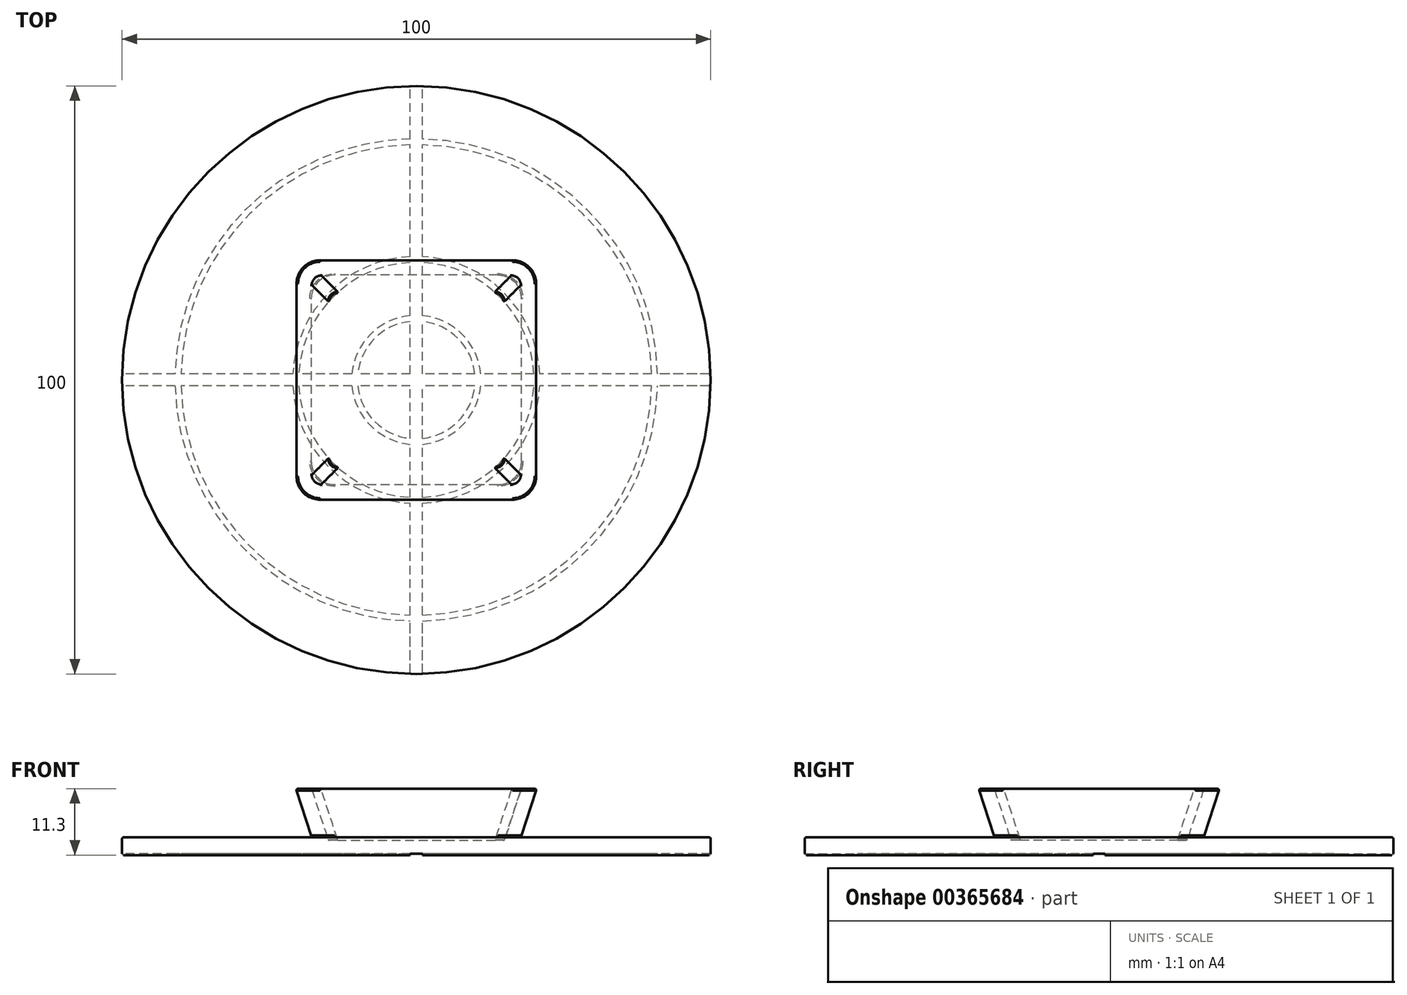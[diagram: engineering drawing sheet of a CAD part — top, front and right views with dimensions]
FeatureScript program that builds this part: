
annotation { "Feature Type Name" : "Feature", "Feature Type Description" : "" }
export const myFeature = defineFeature(function(context is Context, id is Id, definition is map)
    precondition{}
    {
        {
            var Q0;
            Q0=qCreatedBy(makeId("Top.planeOp"),FACE);
            cPlane(context, id + "F0", {"entities" : qUnion([Q0]), "cplaneType" : CPlaneType.OFFSET, "offset" : 8.3 * mm, "width" : 150 * mm, "height" : 150 * mm});
        }
        {
            var Q0;
            Q0=qCreatedBy(makeId("Top.planeOp"),FACE);
            var sketch = newSketch(context, id + "F1", { "sketchPlane" : qUnion([Q0])});
            skLineSegment(sketch, "E0.bottom", {"start": v(-13.75, 17.75) * mm, "end": v(13.75, 17.75) * mm});
            skLineSegment(sketch, "E0.top", {"start": v(-13.75, -17.75) * mm, "end": v(13.75, -17.75) * mm});
            skLineSegment(sketch, "E0.left", {"start": v(-17.75, 13.75) * mm, "end": v(-17.75, -13.75) * mm});
            skLineSegment(sketch, "E0.right", {"start": v(17.75, 13.75) * mm, "end": v(17.75, -13.75) * mm});
            skPoint(sketch, "E0.middle", {"position": v(0, 0) * mm});
            skPoint(sketch, "E1.visualSharp", {"position": v(-17.75, 17.75) * mm});
            skArc(sketch, "E1.filletArc", {"start": v(-13.75, 17.75) * mm, "mid": v(-16.58, 16.58) * mm, "end": v(-17.75, 13.75) * mm});
            skPoint(sketch, "E2.visualSharp", {"position": v(17.75, 17.75) * mm});
            skArc(sketch, "E2.filletArc", {"start": v(17.75, 13.75) * mm, "mid": v(16.58, 16.58) * mm, "end": v(13.75, 17.75) * mm});
            skPoint(sketch, "E3.visualSharp", {"position": v(17.75, -17.75) * mm});
            skArc(sketch, "E3.filletArc", {"start": v(13.75, -17.75) * mm, "mid": v(16.58, -16.58) * mm, "end": v(17.75, -13.75) * mm});
            skPoint(sketch, "E4.visualSharp", {"position": v(-17.75, -17.75) * mm});
            skArc(sketch, "E4.filletArc", {"start": v(-17.75, -13.75) * mm, "mid": v(-16.58, -16.58) * mm, "end": v(-13.75, -17.75) * mm});
            skSolve(sketch);
        }
        {
            var Q0;
            Q0=qCreatedBy(id+"F0.planeOp",FACE);
            var sketch = newSketch(context, id + "F2", { "sketchPlane" : qUnion([Q0])});
            skLineSegment(sketch, "E5.bottom", {"start": v(-16.45, 20.45) * mm, "end": v(16.45, 20.45) * mm});
            skLineSegment(sketch, "E5.top", {"start": v(-16.45, -20.45) * mm, "end": v(16.45, -20.45) * mm});
            skLineSegment(sketch, "E5.left", {"start": v(-20.45, 16.45) * mm, "end": v(-20.45, -16.45) * mm});
            skLineSegment(sketch, "E5.right", {"start": v(20.45, 16.45) * mm, "end": v(20.45, -16.45) * mm});
            skPoint(sketch, "E5.middle", {"position": v(0, 0) * mm});
            skPoint(sketch, "E6.visualSharp", {"position": v(-20.45, 20.45) * mm});
            skArc(sketch, "E6.filletArc", {"start": v(-16.45, 20.45) * mm, "mid": v(-19.28, 19.28) * mm, "end": v(-20.45, 16.45) * mm});
            skPoint(sketch, "E7.visualSharp", {"position": v(20.45, 20.45) * mm});
            skArc(sketch, "E7.filletArc", {"start": v(20.45, 16.45) * mm, "mid": v(19.28, 19.28) * mm, "end": v(16.45, 20.45) * mm});
            skPoint(sketch, "E8.visualSharp", {"position": v(20.45, -20.45) * mm});
            skArc(sketch, "E8.filletArc", {"start": v(16.45, -20.45) * mm, "mid": v(19.28, -19.28) * mm, "end": v(20.45, -16.45) * mm});
            skPoint(sketch, "E9.visualSharp", {"position": v(-20.45, -20.45) * mm});
            skArc(sketch, "E9.filletArc", {"start": v(-20.45, -16.45) * mm, "mid": v(-19.28, -19.28) * mm, "end": v(-16.45, -20.45) * mm});
            skSolve(sketch);
        }
        {
            var Q0;
            Q0 = qSketchRegion(id + "F1", true);
            var Q1;
            Q1 = qSketchRegion(id + "F2", true);
            loft(context, id + "F3", {"sheetProfilesArray" : [{ "sheetProfileEntities" : qUnion([Q0]) }, { "sheetProfileEntities" : qUnion([Q1]) }]});
        }
        {
            var Q0;
            Q0=qCreatedBy(makeId("Top.planeOp"),FACE);
            var sketch = newSketch(context, id + "F4", { "sketchPlane" : qUnion([Q0])});
            skCircle(sketch, "E10", {"center": v(0, 0) * mm, "radius": 50 * mm});
            skSolve(sketch);
        }
        {
            var Q0;
            Q0 = qSketchRegion(id + "F4", true);
            extrude(context, id + "F5", {"entities" : qUnion([Q0]), "operationType" : NewBodyOperationType.ADD, "oppositeDirection" : true, "depth" : 3 * mm});
        }
        {
            var Q0;
            Q0=makeQuery(id+"F3.opLoft","CAP_FACE",FACE,{"disambiguationData":[OSD([makeQuery(id+"F2.imprint","IMPRINT",FACE,{"disambiguationData":[TD([[makeQuery(id+"F2.imprint","IMPRINT",EDGE,{"derivedFrom":sQuery(id+"F2.wireOp",EDGE,"E5.bottom")}),-1.0]])]})])],"isStart":true});
            shell(context, id + "F6", {"entities" : qUnion([Q0]), "thickness" : 2.5 * mm});
        }
        {
            var Q0;
            Q0=makeQuery(id+"F3.opLoft","CAP_FACE",FACE,{"disambiguationData":[OSD([makeQuery(id+"F2.imprint","IMPRINT",FACE,{"disambiguationData":[TD([[makeQuery(id+"F2.imprint","IMPRINT",EDGE,{"derivedFrom":sQuery(id+"F2.wireOp",EDGE,"E5.bottom")}),-1.0]])]})])],"isStart":true});
            var Q1;
            Q1=makeQuery(id+"F5.opExtrude","CAP_FACE",FACE,{"disambiguationData":[OSD([sQuery(id+"F4.wireOp",EDGE,"E10")])],"isStart":true});
            var Q2;
            Q2=makeQuery(id+"F5.opExtrude","CAP_FACE",FACE,{"disambiguationData":[OSD([sQuery(id+"F4.wireOp",EDGE,"E10")])],"isStart":false});
            var Q3;
            Q3=makeQuery(id+"F6.opShell","OFFSET_FACE",FACE,{"disambiguationData":[OSD([sQuery(id+"F4.wireOp",EDGE,"E10")])]});
            fillet(context, id + "F7", {"entities" : qUnion([Q0, Q1, Q2, Q3]), "radius" : .25 * mm, "tangentPropagation" : true, "allowEdgeOverflow" : false});
        }
        {
            var Q0;
            Q0=makeQuery(id+"F5.opExtrude","CAP_FACE",FACE,{"disambiguationData":[OSD([sQuery(id+"F4.wireOp",EDGE,"E10")])],"isStart":false});
            cPlane(context, id + "F8", {"entities" : qUnion([Q0]), "cplaneType" : CPlaneType.OFFSET, "offset" : .25 * mm, "oppositeDirection" : true, "width" : 150 * mm, "height" : 150 * mm});
        }
        {
            var Q0;
            Q0=qCreatedBy(id+"F8.planeOp",FACE);
            var sketch = newSketch(context, id + "F9", { "sketchPlane" : qUnion([Q0])});
            skArc(sketch, "E11", {"start": v(-9.95, -1) * mm, "mid": v(-7.09, -7.06) * mm, "end": v(-1.04, -9.95) * mm});
            skArc(sketch, "E12", {"start": v(-10.95, -1) * mm, "mid": v(-7.8, -7.76) * mm, "end": v(-1.04, -10.95) * mm});
            skLineSegment(sketch, "E13.bottom", {"start": v(-1.04, 55) * mm, "end": v(1.04, 55) * mm});
            skLineSegment(sketch, "E13.top", {"start": v(-1.04, -55) * mm, "end": v(1.04, -55) * mm});
            skLineSegment(sketch, "E13.left", {"start": v(-1.04, 55) * mm, "end": v(-1.04, 40.99) * mm});
            skLineSegment(sketch, "E13.right", {"start": v(1.04, 55) * mm, "end": v(1.04, 40.99) * mm});
            skLineSegment(sketch, "E14.bottom", {"start": v(55, -1) * mm, "end": v(40.99, -1) * mm});
            skLineSegment(sketch, "E14.top", {"start": v(55, 1) * mm, "end": v(40.99, 1) * mm});
            skLineSegment(sketch, "E14.left", {"start": v(55, -1) * mm, "end": v(55, 1) * mm});
            skLineSegment(sketch, "E14.right", {"start": v(-55, -1) * mm, "end": v(-55, 1) * mm});
            skArc(sketch, "E15", {"start": v(-19.97, -1) * mm, "mid": v(-14.16, -14.13) * mm, "end": v(-1.04, -19.97) * mm});
            skArc(sketch, "E16", {"start": v(-20.98, -1) * mm, "mid": v(-14.86, -14.84) * mm, "end": v(-1.04, -20.97) * mm});
            skArc(sketch, "E17", {"start": v(-39.99, -1) * mm, "mid": v(-28.3, -28.27) * mm, "end": v(-1.04, -39.99) * mm});
            skArc(sketch, "E18", {"start": v(-40.99, -1) * mm, "mid": v(-29, -28.98) * mm, "end": v(-1.04, -40.99) * mm});
            skLineSegment(sketch, "E19.trimOffspring", {"start": v(-40.99, 1) * mm, "end": v(-55, 1) * mm});
            skLineSegment(sketch, "E20.trimOffspring", {"start": v(-40.99, -1) * mm, "end": v(-55, -1) * mm});
            skLineSegment(sketch, "E21.trimOffspring", {"start": v(-20.98, -1) * mm, "end": v(-39.99, -1) * mm});
            skLineSegment(sketch, "E22.trimOffspring", {"start": v(-20.98, 1) * mm, "end": v(-39.99, 1) * mm});
            skLineSegment(sketch, "E23.trimOffspring", {"start": v(-10.95, 1) * mm, "end": v(-19.97, 1) * mm});
            skLineSegment(sketch, "E24.trimOffspring", {"start": v(-10.95, -1) * mm, "end": v(-19.97, -1) * mm});
            skArc(sketch, "E25.trimOffspring", {"start": v(1.04, -40.99) * mm, "mid": v(29, -28.98) * mm, "end": v(40.99, -1) * mm});
            skLineSegment(sketch, "E26.trimOffspring", {"start": v(-1.04, -40.99) * mm, "end": v(-1.04, -55) * mm});
            skArc(sketch, "E27.trimOffspring", {"start": v(1.04, -39.99) * mm, "mid": v(28.3, -28.27) * mm, "end": v(39.99, -1) * mm});
            skLineSegment(sketch, "E28.trimOffspring", {"start": v(1.04, -40.99) * mm, "end": v(1.04, -55) * mm});
            skLineSegment(sketch, "E29.trimOffspring", {"start": v(1.04, -20.97) * mm, "end": v(1.04, -39.99) * mm});
            skLineSegment(sketch, "E30.trimOffspring", {"start": v(-1.04, -20.97) * mm, "end": v(-1.04, -39.99) * mm});
            skArc(sketch, "E31.trimOffspring", {"start": v(1.04, -19.97) * mm, "mid": v(14.16, -14.13) * mm, "end": v(19.97, -1) * mm});
            skArc(sketch, "E32.trimOffspring", {"start": v(1.04, -20.97) * mm, "mid": v(14.86, -14.84) * mm, "end": v(20.98, -1) * mm});
            skLineSegment(sketch, "E33.trimOffspring", {"start": v(-1.04, -1) * mm, "end": v(-9.95, -1) * mm});
            skLineSegment(sketch, "E34.trimOffspring", {"start": v(-1.04, 1) * mm, "end": v(-9.95, 1) * mm});
            skLineSegment(sketch, "E35.trimOffspring", {"start": v(-1.04, -1) * mm, "end": v(-1.04, -9.95) * mm});
            skLineSegment(sketch, "E36.trimOffspring", {"start": v(1.04, -1) * mm, "end": v(1.04, -9.95) * mm});
            skArc(sketch, "E37.trimOffspring", {"start": v(1.04, -9.95) * mm, "mid": v(7.09, -7.06) * mm, "end": v(9.95, -1) * mm});
            skArc(sketch, "E38.trimOffspring", {"start": v(1.04, -10.95) * mm, "mid": v(7.8, -7.76) * mm, "end": v(10.95, -1) * mm});
            skLineSegment(sketch, "E39.trimOffspring", {"start": v(-1.04, -10.95) * mm, "end": v(-1.04, -19.97) * mm});
            skLineSegment(sketch, "E40.trimOffspring", {"start": v(1.04, -10.95) * mm, "end": v(1.04, -19.97) * mm});
            skLineSegment(sketch, "E41.trimOffspring", {"start": v(9.95, -1) * mm, "end": v(1.04, -1) * mm});
            skLineSegment(sketch, "E42.trimOffspring", {"start": v(9.95, 1) * mm, "end": v(1.04, 1) * mm});
            skArc(sketch, "E43.trimOffspring", {"start": v(9.95, 1) * mm, "mid": v(7.09, 7.06) * mm, "end": v(1.04, 9.95) * mm});
            skArc(sketch, "E44.trimOffspring", {"start": v(10.95, 1) * mm, "mid": v(7.8, 7.76) * mm, "end": v(1.04, 10.95) * mm});
            skArc(sketch, "E45.trimOffspring", {"start": v(20.98, 1) * mm, "mid": v(14.86, 14.84) * mm, "end": v(1.04, 20.97) * mm});
            skArc(sketch, "E46.trimOffspring", {"start": v(19.97, 1) * mm, "mid": v(14.16, 14.13) * mm, "end": v(1.04, 19.97) * mm});
            skLineSegment(sketch, "E47.trimOffspring", {"start": v(19.97, -1) * mm, "end": v(10.95, -1) * mm});
            skLineSegment(sketch, "E48.trimOffspring", {"start": v(19.97, 1) * mm, "end": v(10.95, 1) * mm});
            skLineSegment(sketch, "E49.trimOffspring", {"start": v(39.99, -1) * mm, "end": v(20.98, -1) * mm});
            skArc(sketch, "E50.trimOffspring", {"start": v(40.99, 1) * mm, "mid": v(29, 28.98) * mm, "end": v(1.04, 40.99) * mm});
            skArc(sketch, "E51.trimOffspring", {"start": v(39.99, 1) * mm, "mid": v(28.3, 28.27) * mm, "end": v(1.04, 39.99) * mm});
            skLineSegment(sketch, "E52.trimOffspring", {"start": v(39.99, 1) * mm, "end": v(20.98, 1) * mm});
            skArc(sketch, "E53.trimOffspring", {"start": v(-1.04, 40.99) * mm, "mid": v(-29, 28.98) * mm, "end": v(-40.99, 1) * mm});
            skArc(sketch, "E54.trimOffspring", {"start": v(-1.04, 39.99) * mm, "mid": v(-28.3, 28.27) * mm, "end": v(-39.99, 1) * mm});
            skLineSegment(sketch, "E55.trimOffspring", {"start": v(-1.04, 39.99) * mm, "end": v(-1.04, 20.97) * mm});
            skLineSegment(sketch, "E56.trimOffspring", {"start": v(1.04, 39.99) * mm, "end": v(1.04, 20.97) * mm});
            skArc(sketch, "E57.trimOffspring", {"start": v(-1.04, 19.97) * mm, "mid": v(-14.16, 14.13) * mm, "end": v(-19.97, 1) * mm});
            skArc(sketch, "E58.trimOffspring", {"start": v(-1.04, 20.97) * mm, "mid": v(-14.86, 14.84) * mm, "end": v(-20.98, 1) * mm});
            skLineSegment(sketch, "E59.trimOffspring", {"start": v(1.04, 19.97) * mm, "end": v(1.04, 10.95) * mm});
            skLineSegment(sketch, "E60.trimOffspring", {"start": v(-1.04, 19.97) * mm, "end": v(-1.04, 10.95) * mm});
            skLineSegment(sketch, "E61.trimOffspring", {"start": v(1.04, 9.95) * mm, "end": v(1.04, 1) * mm});
            skArc(sketch, "E62.trimOffspring", {"start": v(-1.04, 10.95) * mm, "mid": v(-7.8, 7.76) * mm, "end": v(-10.95, 1) * mm});
            skArc(sketch, "E63.trimOffspring", {"start": v(-1.04, 9.95) * mm, "mid": v(-7.09, 7.06) * mm, "end": v(-9.95, 1) * mm});
            skLineSegment(sketch, "E64.trimOffspring", {"start": v(-1.04, 9.95) * mm, "end": v(-1.04, 1) * mm});
            skSolve(sketch);
        }
        {
            var Q0;
            Q0 = qSketchRegion(id + "F9", true);
            extrude(context, id + "F10", {"entities" : qUnion([Q0]), "operationType" : NewBodyOperationType.REMOVE, "depth" : 25 * mm});
        }
    });
